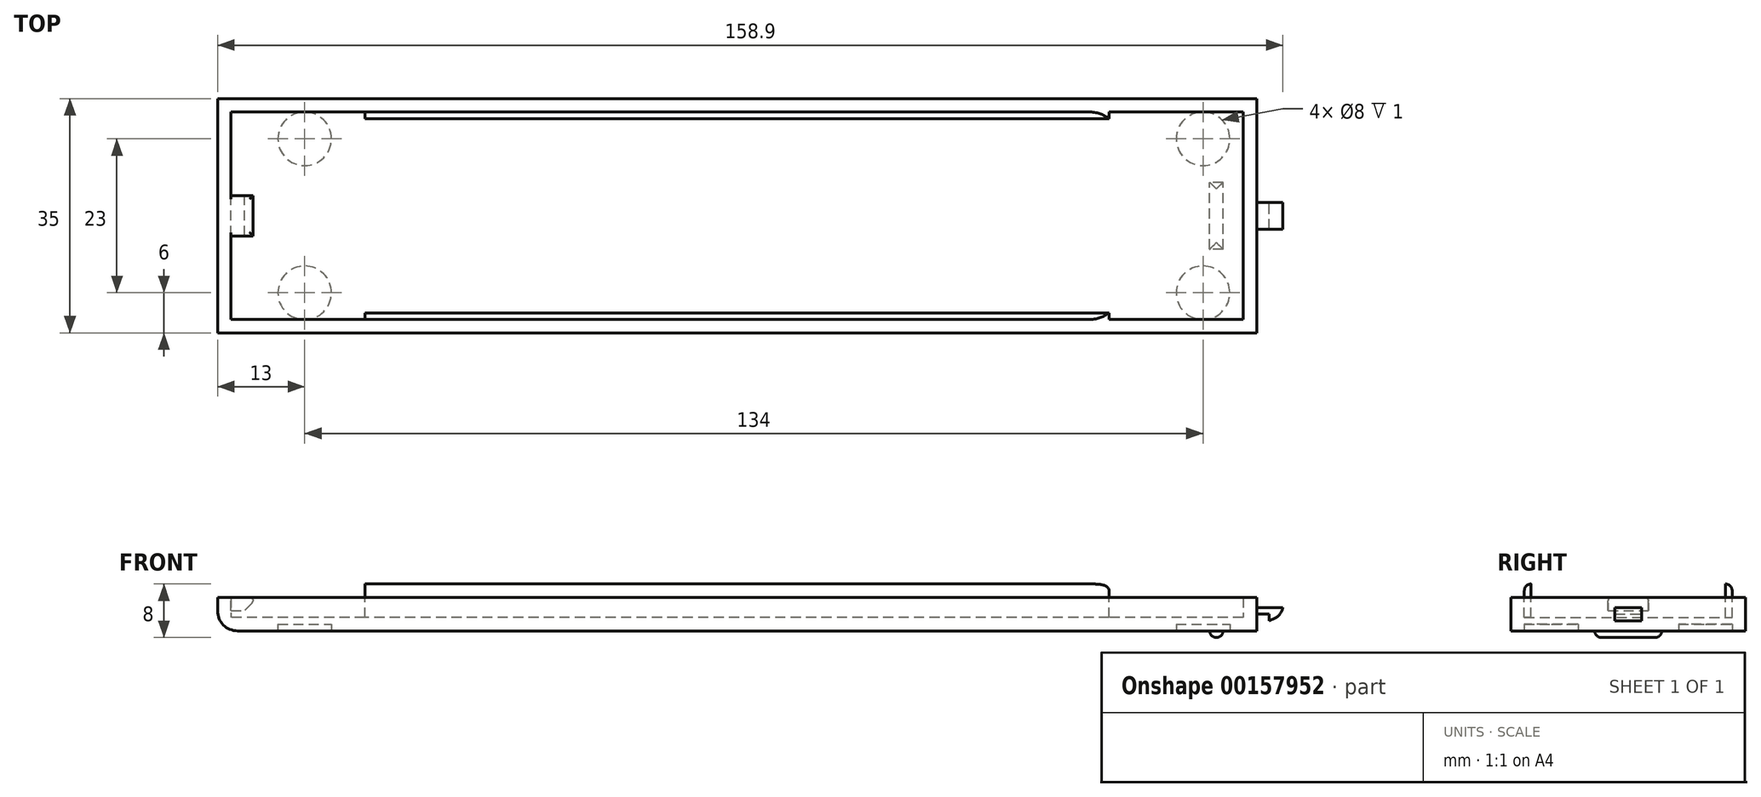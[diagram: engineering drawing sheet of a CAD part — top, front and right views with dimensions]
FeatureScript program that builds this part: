
annotation { "Feature Type Name" : "Feature", "Feature Type Description" : "" }
export const myFeature = defineFeature(function(context is Context, id is Id, definition is map)
    precondition{}
    {
        {
            var Q0;
            Q0=qCreatedBy(makeId("Right.planeOp"),FACE);
            var sketch = newSketch(context, id + "F0", { "sketchPlane" : qUnion([Q0])});
            skLineSegment(sketch, "E0.bottom", {"start": v(-17.5, 2.5) * mm, "end": v(17.5, 2.5) * mm});
            skLineSegment(sketch, "E0.top", {"start": v(-17.5, -2.5) * mm, "end": v(17.5, -2.5) * mm});
            skLineSegment(sketch, "E0.left", {"start": v(-17.5, 2.5) * mm, "end": v(-17.5, -2.5) * mm});
            skLineSegment(sketch, "E0.right", {"start": v(17.5, 2.5) * mm, "end": v(17.5, -2.5) * mm});
            skPoint(sketch, "E0.middle", {"position": v(0, 0) * mm});
            skSolve(sketch);
        }
        {
            var Q0;
            Q0=qSketchRegion(id+"F0",true);
            extrude(context, id + "F1", {"entities" : qUnion([Q0]), "endBound" : BoundingType.SYMMETRIC, "depth" : 155 * mm});
        }
        {
            var Q0;
            Q0=makeQuery(id+"F1.opExtrude","SWEPT_FACE",FACE,{"disambiguationData":[OSD([sQuery(id+"F0.wireOp",EDGE,"E0.bottom")])]});
            shell(context, id + "F2", {"entities" : qUnion([Q0]), "thickness" : 2 * mm});
        }
        {
            var Q0;
            Q0=qCreatedBy(makeId("Front.planeOp"),FACE);
            var sketch = newSketch(context, id + "F3", { "sketchPlane" : qUnion([Q0])});
            skLineSegment(sketch, "E1", {"start": v(-75.5, 2.5) * mm, "end": v(-71.5, 2.5) * mm});
            skLineSegment(sketch, "E2", {"start": v(-75.5, 0.5) * mm, "end": v(-75.5, 2.5) * mm});
            skLineSegment(sketch, "E3", {"start": v(-75.5, 0.5) * mm, "end": v(-73.5, 0.5) * mm});
            skLineSegment(sketch, "E4", {"start": v(-71.5, 2.5) * mm, "end": v(-73.5, 0.5) * mm});
            skPoint(sketch, "E5", {"position": v(-75.5, 2.5) * mm});
            skSolve(sketch);
        }
        {
            var Q0;
            Q0=qSketchRegion(id+"F3",true);
            extrude(context, id + "F4", {"entities" : qUnion([Q0]), "operationType" : NewBodyOperationType.ADD, "endBound" : BoundingType.SYMMETRIC, "depth" : 6 * mm});
        }
        {
            var Q0;
            Q0=qCreatedBy(makeId("Front.planeOp"),FACE);
            var sketch = newSketch(context, id + "F5", { "sketchPlane" : qUnion([Q0])});
            skLineSegment(sketch, "E6.bottom", {"start": v(77.5, 1) * mm, "end": v(81.4, 1) * mm});
            skLineSegment(sketch, "E6.top", {"start": v(77.5, 0) * mm, "end": v(81.4, 0) * mm});
            skLineSegment(sketch, "E6.left", {"start": v(77.5, 1) * mm, "end": v(77.5, 0) * mm});
            skLineSegment(sketch, "E6.right", {"start": v(81.4, 1) * mm, "end": v(81.4, 0) * mm});
            skLineSegment(sketch, "E7", {"start": v(81.4, 0) * mm, "end": v(79.4, -1) * mm});
            skLineSegment(sketch, "E8", {"start": v(79.4, -1) * mm, "end": v(79.4, 0) * mm});
            skSolve(sketch);
        }
        {
            var Q0;
            Q0=makeQuery(id+"F5.imprint","IMPRINT",FACE,{"disambiguationData":[TD([[makeQuery(id+"F5.imprint","IMPRINT",EDGE,{"derivedFrom":sQuery(id+"F5.wireOp",EDGE,"E6.bottom")}),-1.0]])]});
            var Q1;
            {var subQ0=sQuery(id+"F5.wireOp",EDGE,"E7");Q1=makeQuery(id+"F5.imprint","IMPRINT",FACE,{"disambiguationData":[TD([[makeQuery(id+"F5.imprint","IMPRINT",EDGE,{"derivedFrom":subQ0}),-1.0]])]});}
            extrude(context, id + "F6", {"entities" : qUnion([Q0, Q1]), "operationType" : NewBodyOperationType.ADD, "endBound" : BoundingType.SYMMETRIC, "depth" : 4 * mm});
        }
        {
            var Q0;
            Q0=makeQuery(id+"F6.opExtrude","SWEPT_EDGE",EDGE,{"disambiguationData":[OSD([sQuery(id+"F5.wireOp",EDGE,"E6.top"),sQuery(id+"F5.wireOp",EDGE,"E6.right"),sQuery(id+"F5.wireOp",EDGE,"E7")])]});
            fillet(context, id + "F7", {"entities" : qUnion([Q0]), "radius" : 2 * mm, "tangentPropagation" : true, "allowEdgeOverflow" : false});
        }
        {
            var Q0;
            Q0=makeQuery(id+"F2.opShell","OFFSET_FACE",FACE,{"disambiguationData":[OSD([sQuery(id+"F0.wireOp",EDGE,"E0.left")])]});
            var sketch = newSketch(context, id + "F8", { "sketchPlane" : qUnion([Q0])});
            skLineSegment(sketch, "E9.bottom", {"start": v(-55.5, -0.5) * mm, "end": v(55.5, -0.5) * mm});
            skLineSegment(sketch, "E9.top", {"start": v(-55.5, 4.5) * mm, "end": v(55.5, 4.5) * mm});
            skLineSegment(sketch, "E9.left", {"start": v(-55.5, -0.5) * mm, "end": v(-55.5, 4.5) * mm});
            skLineSegment(sketch, "E9.right", {"start": v(55.5, -0.5) * mm, "end": v(55.5, 4.5) * mm});
            skSolve(sketch);
        }
        {
            var Q0;
            Q0=qSketchRegion(id+"F8",true);
            extrude(context, id + "F9", {"entities" : qUnion([Q0]), "operationType" : NewBodyOperationType.ADD, "depth" : 1 * mm});
        }
        {
            var Q0;
            Q0=makeQuery(id+"F2.opShell","OFFSET_FACE",FACE,{"disambiguationData":[OSD([sQuery(id+"F0.wireOp",EDGE,"E0.right")])]});
            var sketch = newSketch(context, id + "F10", { "sketchPlane" : qUnion([Q0])});
            skLineSegment(sketch, "E10.bottom", {"start": v(-55.5, -0.5) * mm, "end": v(55.5, -0.5) * mm});
            skLineSegment(sketch, "E10.top", {"start": v(-55.5, 4.5) * mm, "end": v(55.5, 4.5) * mm});
            skLineSegment(sketch, "E10.left", {"start": v(-55.5, -0.5) * mm, "end": v(-55.5, 4.5) * mm});
            skLineSegment(sketch, "E10.right", {"start": v(55.5, -0.5) * mm, "end": v(55.5, 4.5) * mm});
            skSolve(sketch);
        }
        {
            var Q0;
            {var subQ0=sQuery(id+"F10.wireOp",EDGE,"E10.top");Q0=makeQuery(id+"F10.imprint","IMPRINT",FACE,{"disambiguationData":[TD([[makeQuery(id+"F10.imprint","IMPRINT",EDGE,{"derivedFrom":subQ0}),-1.0]])]});}
            var Q1;
            {var subQ0=sQuery(id+"F10.wireOp",EDGE,"E10.bottom");Q1=makeQuery(id+"F10.imprint","IMPRINT",FACE,{"disambiguationData":[TD([[makeQuery(id+"F10.imprint","IMPRINT",EDGE,{"derivedFrom":subQ0}),-1.0]])]});}
            var Q2;
            Q2=sQuery(id+"F10.wireOp",EDGE,"E10.bottom");
            var Q3;
            Q3=sQuery(id+"F10.wireOp",EDGE,"E10.left");
            var Q4;
            Q4=sQuery(id+"F10.wireOp",EDGE,"E10.top");
            var Q5;
            Q5=sQuery(id+"F10.wireOp",EDGE,"E10.right");
            extrude(context, id + "F11", {"entities" : qUnion([Q0, Q1]), "operationType" : NewBodyOperationType.ADD, "surfaceEntities" : qUnion([Q2, Q3, Q4, Q5]), "depth" : 1 * mm});
        }
        {
            var Q0;
            {var subQ0=sQuery(id+"F10.wireOp",EDGE,"E10.right");Q0=makeQuery(id+"F11.boolean.opBoolean","SPLIT",EDGE,{"disambiguationData":[topologyDisambiguationEdgeConnected([makeQuery(id+"F11.opExtrude","CAP_FACE",FACE,{"disambiguationData":[OSD([sQuery(id+"F10.wireOp",EDGE,"E10.bottom"),sQuery(id+"F10.wireOp",EDGE,"E10.top"),sQuery(id+"F10.wireOp",EDGE,"E10.left"),subQ0])],"isStart":true})])],"derivedFrom":makeQuery(id+"F11.opExtrude","CAP_EDGE",EDGE,{"disambiguationData":[OSD([subQ0])],"isStart":true})});}
            var Q1;
            {var subQ0=sQuery(id+"F8.wireOp",EDGE,"E9.left");Q1=makeQuery(id+"F9.boolean.opBoolean","SPLIT",EDGE,{"disambiguationData":[topologyDisambiguationEdgeConnected([makeQuery(id+"F9.opExtrude","CAP_FACE",FACE,{"disambiguationData":[OSD([sQuery(id+"F8.wireOp",EDGE,"E9.bottom"),sQuery(id+"F8.wireOp",EDGE,"E9.top"),subQ0,sQuery(id+"F8.wireOp",EDGE,"E9.right")])],"isStart":true})])],"derivedFrom":makeQuery(id+"F9.opExtrude","CAP_EDGE",EDGE,{"disambiguationData":[OSD([subQ0])],"isStart":true})});}
            fillet(context, id + "F12", {"entities" : qUnion([Q0, Q1]), "radius" : 5 * mm, "tangentPropagation" : true, "allowEdgeOverflow" : false});
        }
        {
            var Q0;
            Q0=makeQuery(id+"F9.opExtrude","CAP_EDGE",EDGE,{"disambiguationData":[OSD([sQuery(id+"F8.wireOp",EDGE,"E9.top")])],"isStart":true});
            var Q1;
            Q1=makeQuery(id+"F11.opExtrude","CAP_EDGE",EDGE,{"disambiguationData":[OSD([sQuery(id+"F10.wireOp",EDGE,"E10.top")])],"isStart":true});
            fillet(context, id + "F13", {"entities" : qUnion([Q0, Q1]), "radius" : 1 * mm, "tangentPropagation" : true, "allowEdgeOverflow" : false});
        }
        {
            var Q0;
            Q0=makeQuery(id+"F4.opExtrude","SWEPT_EDGE",EDGE,{"disambiguationData":[OSD([sQuery(id+"F3.wireOp",EDGE,"E1"),sQuery(id+"F3.wireOp",EDGE,"E4")])]});
            var Q1;
            Q1=makeQuery(id+"F4.opExtrude","CAP_EDGE",EDGE,{"disambiguationData":[OSD([sQuery(id+"F3.wireOp",EDGE,"E1")])],"isStart":false});
            var Q2;
            Q2=makeQuery(id+"F4.opExtrude","CAP_EDGE",EDGE,{"disambiguationData":[OSD([sQuery(id+"F3.wireOp",EDGE,"E1")])],"isStart":true});
            fillet(context, id + "F14", {"entities" : qUnion([Q0, Q1, Q2]), "radius" : 0.5 * mm, "tangentPropagation" : true, "allowEdgeOverflow" : false});
        }
        {
            var Q0;
            Q0=makeQuery(id+"F1.opExtrude","SWEPT_FACE",FACE,{"disambiguationData":[OSD([sQuery(id+"F0.wireOp",EDGE,"E0.top")])]});
            var sketch = newSketch(context, id + "F15", { "sketchPlane" : qUnion([Q0])});
            skCircle(sketch, "E11", {"center": v(69.5, -11.5) * mm, "radius": 4 * mm});
            skCircle(sketch, "E12", {"center": v(69.5, 11.5) * mm, "radius": 4 * mm});
            skCircle(sketch, "E13", {"center": v(-64.5, -11.5) * mm, "radius": 4 * mm});
            skCircle(sketch, "E14", {"center": v(-64.5, 11.5) * mm, "radius": 4 * mm});
            skSolve(sketch);
        }
        {
            var Q0;
            Q0=makeQuery(id+"F15.imprint","IMPRINT",FACE,{"disambiguationData":[TD([[makeQuery(id+"F15.imprint","IMPRINT",EDGE,{"derivedFrom":sQuery(id+"F15.wireOp",EDGE,"E14")}),1.0]])]});
            var Q1;
            Q1=makeQuery(id+"F15.imprint","IMPRINT",FACE,{"disambiguationData":[TD([[makeQuery(id+"F15.imprint","IMPRINT",EDGE,{"derivedFrom":sQuery(id+"F15.wireOp",EDGE,"E13")}),1.0]])]});
            var Q2;
            Q2=makeQuery(id+"F15.imprint","IMPRINT",FACE,{"disambiguationData":[TD([[makeQuery(id+"F15.imprint","IMPRINT",EDGE,{"derivedFrom":sQuery(id+"F15.wireOp",EDGE,"E11")}),1.0]])]});
            var Q3;
            Q3=makeQuery(id+"F15.imprint","IMPRINT",FACE,{"disambiguationData":[TD([[makeQuery(id+"F15.imprint","IMPRINT",EDGE,{"derivedFrom":sQuery(id+"F15.wireOp",EDGE,"E12")}),1.0]])]});
            var Q4;
            Q4=sQuery(id+"F15.wireOp",EDGE,"E11");
            var Q5;
            Q5=sQuery(id+"F15.wireOp",EDGE,"E13");
            var Q6;
            Q6=sQuery(id+"F15.wireOp",EDGE,"E14");
            var Q7;
            Q7=sQuery(id+"F15.wireOp",EDGE,"E12");
            extrude(context, id + "F16", {"entities" : qUnion([Q0, Q1, Q2, Q3]), "operationType" : NewBodyOperationType.REMOVE, "surfaceEntities" : qUnion([Q4, Q5, Q6, Q7]), "oppositeDirection" : true, "depth" : 1 * mm});
        }
        {
            var Q0;
            Q0=makeQuery(id+"F1.opExtrude","SWEPT_FACE",FACE,{"disambiguationData":[OSD([sQuery(id+"F0.wireOp",EDGE,"E0.top")])]});
            var sketch = newSketch(context, id + "F17", { "sketchPlane" : qUnion([Q0])});
            skLineSegment(sketch, "E15.bottom", {"start": v(72.5, 5) * mm, "end": v(70.5, 5) * mm});
            skLineSegment(sketch, "E15.top", {"start": v(72.5, -5) * mm, "end": v(70.5, -5) * mm});
            skLineSegment(sketch, "E15.left", {"start": v(72.5, 5) * mm, "end": v(72.5, -5) * mm});
            skLineSegment(sketch, "E15.right", {"start": v(70.5, 5) * mm, "end": v(70.5, -5) * mm});
            skPoint(sketch, "E15.middle", {"position": v(71.5, 0) * mm});
            skSolve(sketch);
        }
        {
            var Q0;
            Q0=qSketchRegion(id+"F17",true);
            extrude(context, id + "F18", {"entities" : qUnion([Q0]), "operationType" : NewBodyOperationType.ADD, "depth" : 1 * mm});
        }
        {
            var Q0;
            Q0=makeQuery(id+"F18.opExtrude","CAP_EDGE",EDGE,{"disambiguationData":[OSD([sQuery(id+"F17.wireOp",EDGE,"E15.bottom")])],"isStart":false});
            var Q1;
            Q1=makeQuery(id+"F18.opExtrude","CAP_EDGE",EDGE,{"disambiguationData":[OSD([sQuery(id+"F17.wireOp",EDGE,"E15.left")])],"isStart":false});
            var Q2;
            Q2=makeQuery(id+"F18.opExtrude","CAP_EDGE",EDGE,{"disambiguationData":[OSD([sQuery(id+"F17.wireOp",EDGE,"E15.top")])],"isStart":false});
            var Q3;
            Q3=makeQuery(id+"F18.opExtrude","CAP_EDGE",EDGE,{"disambiguationData":[OSD([sQuery(id+"F17.wireOp",EDGE,"E15.right")])],"isStart":false});
            fillet(context, id + "F19", {"entities" : qUnion([Q0, Q1, Q2, Q3]), "radius" : 1 * mm, "tangentPropagation" : true, "allowEdgeOverflow" : false});
        }
        {
            var Q0;
            Q0=makeQuery(id+"F1.opExtrude","CAP_EDGE",EDGE,{"disambiguationData":[OSD([sQuery(id+"F0.wireOp",EDGE,"E0.top")])],"isStart":true});
            fillet(context, id + "F20", {"entities" : qUnion([Q0]), "radius" : 3 * mm, "tangentPropagation" : true, "allowEdgeOverflow" : false});
        }
    });
